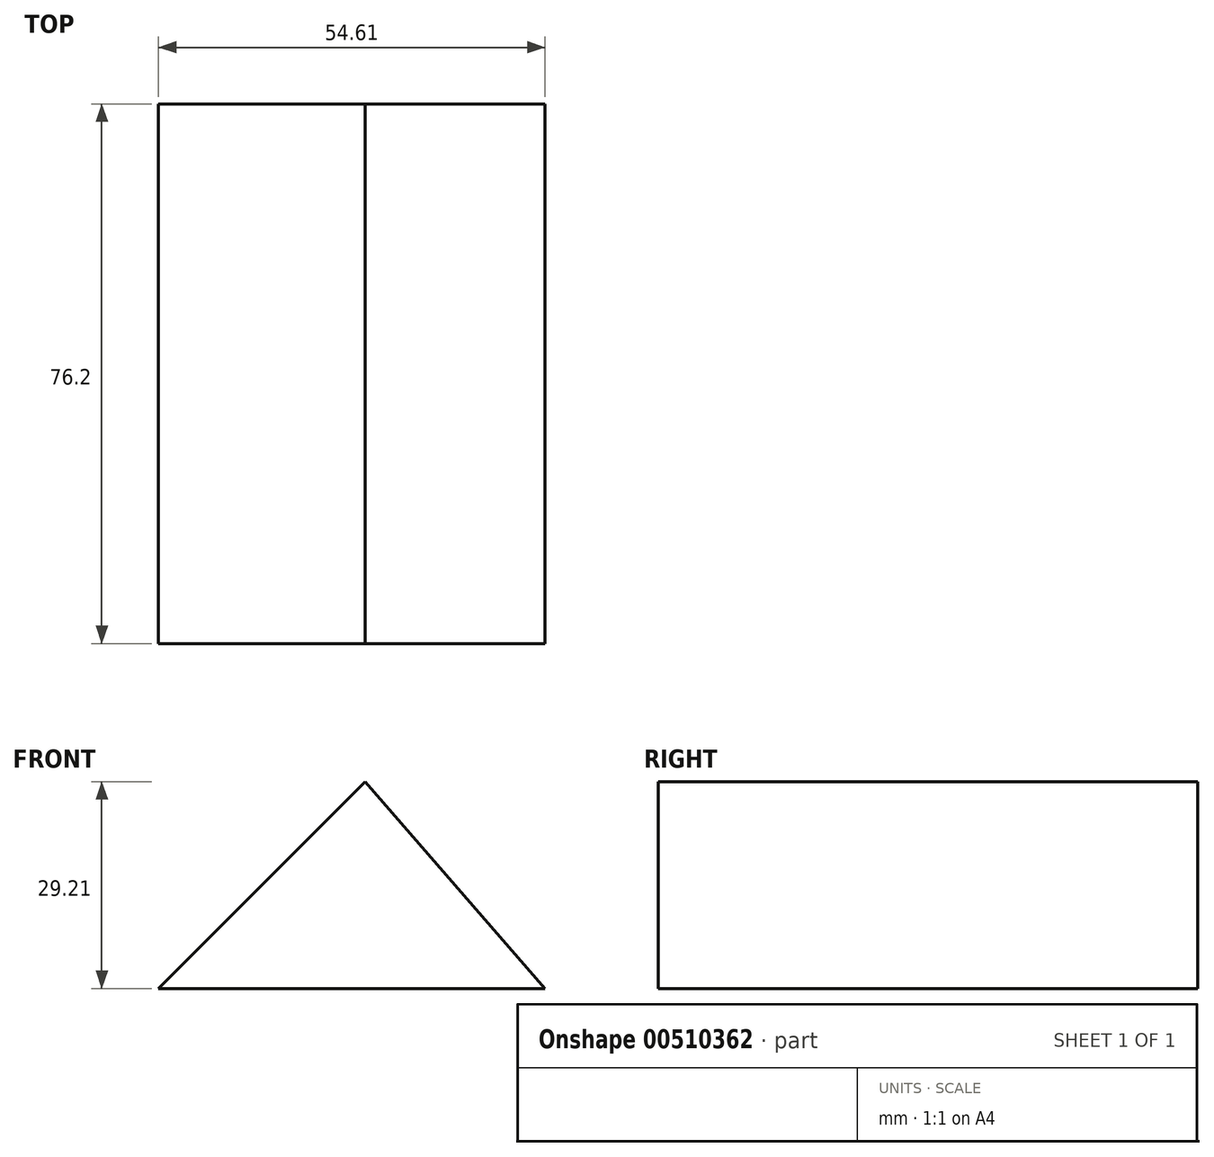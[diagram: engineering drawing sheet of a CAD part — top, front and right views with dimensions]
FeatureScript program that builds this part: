
annotation { "Feature Type Name" : "Feature", "Feature Type Description" : "" }
export const myFeature = defineFeature(function(context is Context, id is Id, definition is map)
    precondition{}
    {
        {
            var Q0;
            Q0=qCreatedBy(makeId("Front.planeOp"),FACE);
            var sketch = newSketch(context, id + "F0", { "sketchPlane" : qUnion([Q0])});
            skLineSegment(sketch, "E0", {"start": v(-32.65, -35.56) * mm, "end": v(21.96, -35.56) * mm});
            skLineSegment(sketch, "E1", {"start": v(21.96, -35.56) * mm, "end": v(-3.44, -35.56) * mm});
            skLineSegment(sketch, "E2", {"start": v(-3.44, -35.56) * mm, "end": v(-3.44, -6.35) * mm});
            skLineSegment(sketch, "E3", {"start": v(21.96, -35.56) * mm, "end": v(-3.44, -6.35) * mm});
            skLineSegment(sketch, "E4", {"start": v(-3.44, -6.35) * mm, "end": v(-32.65, -35.56) * mm});
            skSolve(sketch);
        }
        {
            var Q0;
            Q0=makeQuery(id+"F0.imprint","IMPRINT",FACE,{"disambiguationData":[TD([[makeQuery(id+"F0.imprint","IMPRINT",EDGE,{"derivedFrom":sQuery(id+"F0.wireOp",EDGE,"E0")}),1.0]])]});
            var Q1;
            Q1=makeQuery(id+"F0.imprint","IMPRINT",FACE,{"disambiguationData":[TD([[makeQuery(id+"F0.imprint","IMPRINT",EDGE,{"derivedFrom":sQuery(id+"F0.wireOp",EDGE,"E1")}),-1.0]])]});
            extrude(context, id + "F1", {"entities" : qUnion([Q0, Q1]), "endBound" : BoundingType.SYMMETRIC, "depth" : 76.2 * mm});
        }
    });
